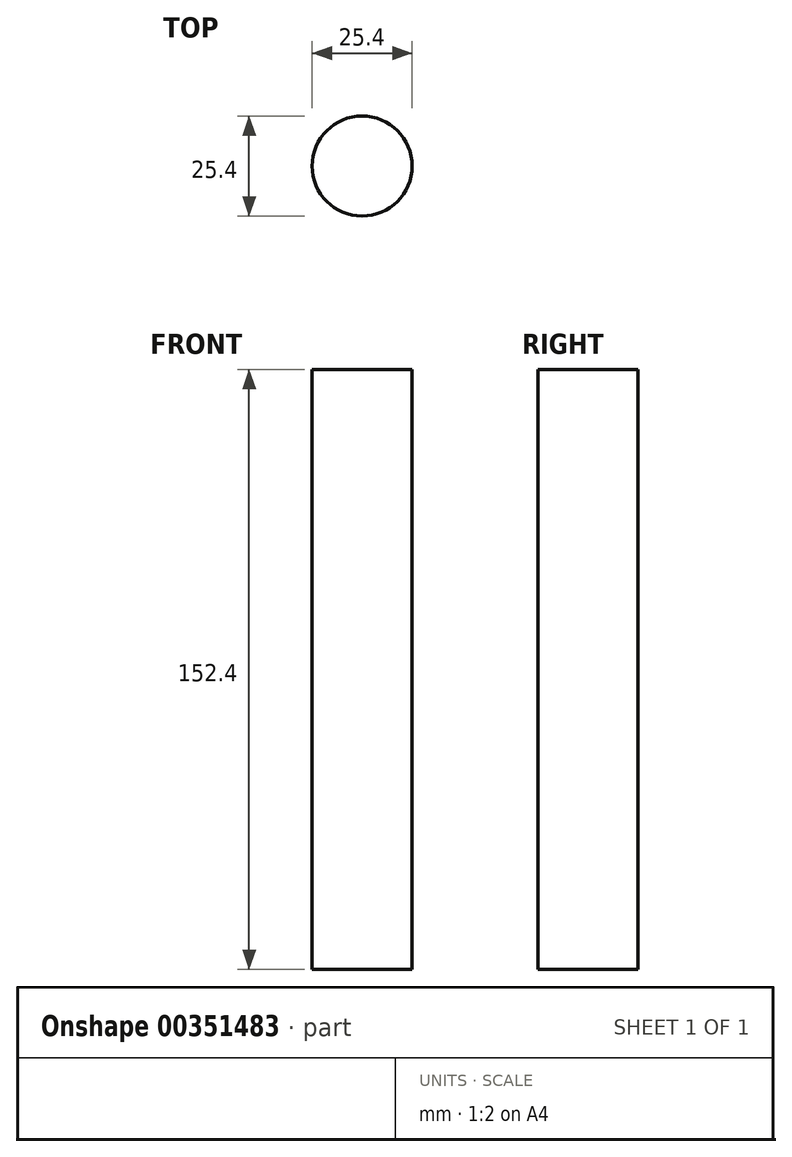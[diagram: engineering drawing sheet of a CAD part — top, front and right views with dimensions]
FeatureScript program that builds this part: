
annotation { "Feature Type Name" : "Feature", "Feature Type Description" : "" }
export const myFeature = defineFeature(function(context is Context, id is Id, definition is map)
    precondition{}
    {
        {
            var Q0;
            Q0=qCreatedBy(makeId("Top.planeOp"),FACE);
            var sketch = newSketch(context, id + "F0", { "sketchPlane" : qUnion([Q0])});
            skCircle(sketch, "E0", {"center": v(0, 0) * mm, "radius": 12.7 * mm});
            skSolve(sketch);
        }
        {
            var Q0;
            Q0 = qSketchRegion(id + "F0", true);
            extrude(context, id + "F1", {"entities" : qUnion([Q0]), "endBound" : BoundingType.SYMMETRIC, "depth" : 152.4 * mm});
        }
    });
